# Revit family: Sarlam_Eclairage_Applique_ECOled_IP44_600Lm
name_source: partatom
category: Dispositifs d'éclairage
units: mm (PartAtom-declared; Revit-internal decimal feet)

## family parameters
Conserver l'orientation des annotations = Oui
Cote de connecteur circulaire = Utiliser le diamètre
Couper avec des vides une fois chargée = Non
Hôte = Face
Partagée = Non
Point de calcul de pièce = Non
Type d'élément = Normal

## types (2) — shared parameters
Adapté à un montage au plafond = Non
Adapté à un montage en applique = Non
Adapté à un montage en saillie = Non
Adapté à un montage encastré = Non
Adapté à une suspension = Non
Angle du faisceau = 0
Appareillage = 0
Avec détecteur crépusculaire = Non
Avec détecteur de mouvement = Non
Classe de protection = II
Condition Générale d'Utilisation = https://export.legrand.com
Couleur du boîtier/corps = LEGRAND - Blanc
Douille = 0
Elévation par défaut = 1800 mm
Fabricant = LEGRAND
Flux lumineux utile lm = 600
Indice de protection (IP) = IP44
Indice de protection contre les chocs (IK) = IK07
Indice de rendu des couleurs CRI = 0
Matériau du boîtier/corps = LEGRAND - Polycarbonate
Répartition lumineuse = 0
URL = http://www.legrandoc.com
zero-valued in all types: Courant nominal mA MAX, Courant nominal mA MIN, Diamètre d'encastrement, Diamètre externe, Hauteur/profondeur, Hauteur/profondeur d'encastrement, Largeur, Largeur d'encastrement, Longueur, Longueur d'encastrement, Puissance du système W, Température de couleur K MAX, Température de couleur K MIN, Tension nominale (Un) V MAX, Tension nominale (Un) V MIN

## per-type parameters (varying)
| type | Description | Modèle |
| ON/OFF | ECOLED 600LM IP44 | SL-189800 |
| Interrupteur | ECOLED 600LM IP44 AVEC INTERRUPTEUR | SL-189801 |

## geometry (parser evidence)
native form markers: Blend x10
no freeform markers — native parametric forms only
